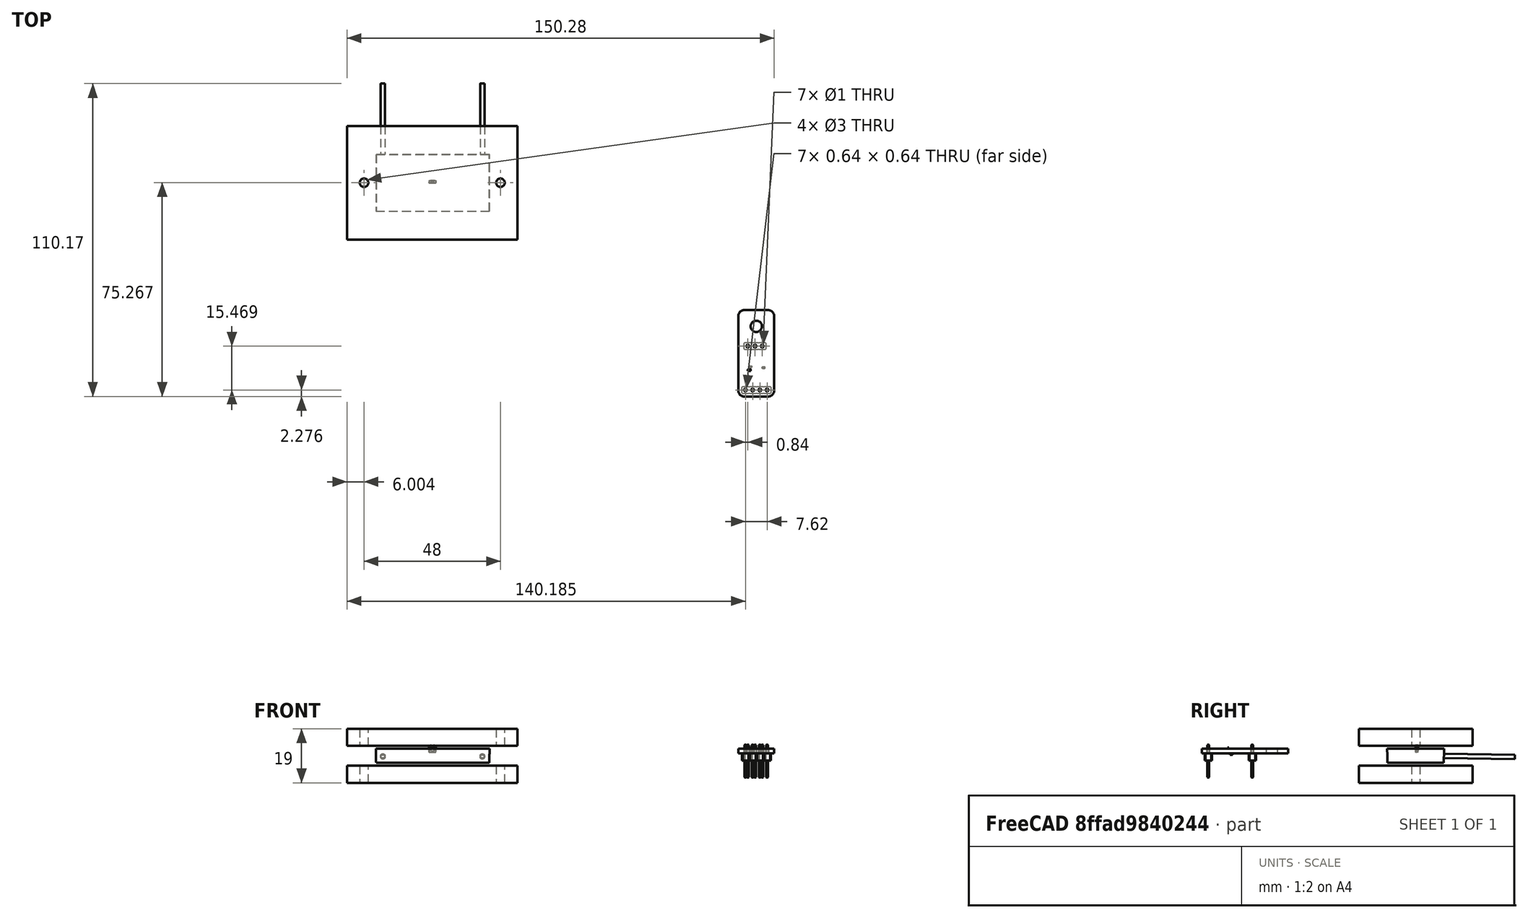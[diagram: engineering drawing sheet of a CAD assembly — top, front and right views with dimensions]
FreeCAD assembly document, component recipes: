
FREECAD ASSEMBLY — COMPONENT RECIPES ("Config-Peltier-SHT-31")

This assembly document has 4 components, labeled P0..P3 below (a component is one placed body or linked part). 3 of them carry a construction recipe — the FreeCAD feature program that regenerates the part from scratch, quoted from this document or its linked companion documents; the rest are supplied as boundary geometry only. No exploded tour is included for this assembly.
COMPONENT P0 — geometry summary ("SHT31-Breakout-rev01"; no construction recipe available for this part):
  bounding box: 30.4 x 12.6 x 3.0 mm
  tessellated surface: 10,052 triangles
  volume: 588 mm^3 (51% of its bounding box)
COMPONENT P1 — recipe-attached ("Placa-Sup", modeled in this document).
Construction recipe (the document's own serialized feature program — sketch geometry with constraints, then the solid features built on it; lengths are millimeters unless a unit is written):

FEATURE [Sketcher::SketchObject] Sketch
  FullyConstrained = true
  MapMode = 5
  Support = -> [XY_Plane]
  sketch-geometry (6):
    g0: Circle CenterX=-24.0764 CenterY=0.06715 CenterZ=0 NormalX=0 NormalY=0 NormalZ=1 AngleXU=0 Radius=1.5
    g1: Circle CenterX=23.9236 CenterY=0.06715 CenterZ=0 NormalX=0 NormalY=0 NormalZ=1 AngleXU=0 Radius=1.5
    g2: LineSegment StartX=-30.0764 StartY=20.0671 StartZ=0 EndX=29.9236 EndY=20.0671 EndZ=0
    g3: LineSegment StartX=29.9236 StartY=20.0671 StartZ=0 EndX=29.9236 EndY=-19.9329 EndZ=0
    g4: LineSegment StartX=29.9236 StartY=-19.9329 StartZ=0 EndX=-30.0764 EndY=-19.9329 EndZ=0
    g5: LineSegment StartX=-30.0764 StartY=-19.9329 StartZ=0 EndX=-30.0764 EndY=20.0671 EndZ=0
  constraints (18):
    c: Diameter(g1) = 3
    c: Diameter(g0) = 3
    c: Distance(g0,g-1) = 0.06715
    c: Coincident(g2,g3)
    c: Coincident(g3,g4)
    c: Coincident(g4,g5)
    c: Coincident(g5,g2)
    c: Horizontal(g2)
    c: Horizontal(g4)
    c: Vertical(g3)
    c: Vertical(g5)
    c: Distance(g3) = 40
    c: Distance(g2) = 60
    c: Distance(g1,g3) = 6
    c: Distance(g1,g2) = 20
    c: Distance(g0,g5) = 6
    c: Distance(g0,g2) = 20
    c: Block(g4)
FEATURE [PartDesign::Pad] Pad
  Direction = (0,0,1)
  Length = 6
  Length2 = 10
  Profile = -> Sketch
  ReferenceAxis = -> Sketch [N_Axis]
  Type = 0
FEATURE [PartDesign::Body] Body  label="Placa-Sup"
  Group = -> [Sketch,Pad]
  Origin = -> Origin
  Placement = pos=(0,0,1) rot=(0,0,1;0rad)
  Tip = -> Pad
COMPONENT P2 — recipe-attached ("Peltier", modeled in this document).
Construction recipe (the document's own serialized feature program — sketch geometry with constraints, then the solid features built on it; lengths are millimeters unless a unit is written):

FEATURE [PartDesign::Plane] DatumPlane
  Length = 60.9515
  MapMode = 5
  Placement = pos=(0,0,0) rot=(1,0,0;3.14159rad)
  ResizeMode = 0
  Width = 70.9193
FEATURE [Sketcher::SketchObject] Sketch002
  FullyConstrained = true
  MapMode = 5
  Placement = pos=(0,0,0) rot=(1,0,0;3.14159rad)
  Support = -> [DatumPlane]
  sketch-geometry (4):
    g0: LineSegment StartX=-19.909 StartY=9.99788 StartZ=0 EndX=20.091 EndY=9.99788 EndZ=0
    g1: LineSegment StartX=20.091 StartY=9.99788 StartZ=0 EndX=20.091 EndY=-10.0021 EndZ=0
    g2: LineSegment StartX=20.091 StartY=-10.0021 StartZ=0 EndX=-19.909 EndY=-10.0021 EndZ=0
    g3: LineSegment StartX=-19.909 StartY=-10.0021 StartZ=0 EndX=-19.909 EndY=9.99788 EndZ=0
  constraints (11):
    c: Coincident(g0,g1)
    c: Coincident(g1,g2)
    c: Coincident(g2,g3)
    c: Coincident(g3,g0)
    c: Horizontal(g0)
    c: Horizontal(g2)
    c: Vertical(g1)
    c: Vertical(g3)
    c: Distance(g0) = 40
    c: Distance(g1) = 20
    c: Block(g2)
FEATURE [PartDesign::Pad] Pad002
  Direction = (0,0,-1)
  Length = 5
  Length2 = 10
  Placement = pos=(0,0,0) rot=(1,0,0;3.14159rad)
  Profile = -> Sketch002
  ReferenceAxis = -> Sketch002 [N_Axis]
  TaperAngle = -1
  Type = 0
FEATURE [PartDesign::Plane] DatumPlane001
  Length = 61.1423
  MapMode = 45
  Placement = pos=(0.0910191,9.95852,-2.49818) rot=(0.58068,0.58068,0.570633;4.17868rad)
  ResizeMode = 0
  Support = -> [Pad002]
  Width = 60.1034
FEATURE [Sketcher::SketchObject] Sketch004
  FullyConstrained = true
  MapMode = 5
  Placement = pos=(0.0910191,9.95852,-2.49818) rot=(0.58068,0.58068,0.570633;4.17868rad)
  Support = -> [DatumPlane001]
  sketch-geometry (2):
    g0: Circle CenterX=0 CenterY=17.4497 CenterZ=0 NormalX=0 NormalY=0 NormalZ=1 AngleXU=0 Radius=0.75
    g1: Circle CenterX=0 CenterY=-17.5503 CenterZ=0 NormalX=0 NormalY=0 NormalZ=1 AngleXU=0 Radius=0.75
  constraints (6):
    c: Diameter(g0) = 1.5
    c: DistanceX(g-2,g0) = 0
    c: Block(g0)
    c: Diameter(g1) = 1.5
    c: DistanceX(g-2,g1) = 0
    c: DistanceY(g1,g0) = 35
FEATURE [PartDesign::Pad] Pad004
  BaseFeature = -> Pad002
  Direction = (0,0.999848,-0.0174524)
  Length = 25
  Length2 = 10
  Placement = pos=(0,0,0) rot=(1,0,0;3.14159rad)
  Profile = -> Sketch004
  ReferenceAxis = -> Sketch004 [N_Axis]
  Type = 0
FEATURE [PartDesign::Body] Body001  label="Peltier"
  Group = -> [DatumPlane,Sketch002,Pad002,DatumPlane001,Sketch004,Pad004]
  Origin = -> Origin001
  Tip = -> Pad004
COMPONENT P3 — recipe-attached ("Placa-Inf", modeled in this document).
Construction recipe (the document's own serialized feature program — sketch geometry with constraints, then the solid features built on it; lengths are millimeters unless a unit is written):

FEATURE [Sketcher::SketchObject] Sketch003
  FullyConstrained = true
  MapMode = 5
  Support = -> [XY_Plane002]
  sketch-geometry (6):
    g0: Circle CenterX=-24.0764 CenterY=0.06715 CenterZ=0 NormalX=0 NormalY=0 NormalZ=1 AngleXU=0 Radius=1.5
    g1: Circle CenterX=23.9236 CenterY=0.06715 CenterZ=0 NormalX=0 NormalY=0 NormalZ=1 AngleXU=0 Radius=1.5
    g2: LineSegment StartX=-30.0764 StartY=20.0671 StartZ=0 EndX=29.9236 EndY=20.0671 EndZ=0
    g3: LineSegment StartX=29.9236 StartY=20.0671 StartZ=0 EndX=29.9236 EndY=-19.9329 EndZ=0
    g4: LineSegment StartX=29.9236 StartY=-19.9329 StartZ=0 EndX=-30.0764 EndY=-19.9329 EndZ=0
    g5: LineSegment StartX=-30.0764 StartY=-19.9329 StartZ=0 EndX=-30.0764 EndY=20.0671 EndZ=0
  constraints (18):
    c: Diameter(g1) = 3
    c: Diameter(g0) = 3
    c: Distance(g0,g-1) = 0.06715
    c: Coincident(g2,g3)
    c: Coincident(g3,g4)
    c: Coincident(g4,g5)
    c: Coincident(g5,g2)
    c: Horizontal(g2)
    c: Horizontal(g4)
    c: Vertical(g3)
    c: Vertical(g5)
    c: Distance(g3) = 40
    c: Distance(g2) = 60
    c: Distance(g1,g3) = 6
    c: Distance(g1,g2) = 20
    c: Distance(g0,g5) = 6
    c: Distance(g0,g2) = 20
    c: Block(g4)
FEATURE [PartDesign::Pad] Pad003
  Direction = (0,0,1)
  Length = 6
  Length2 = 10
  Profile = -> Sketch003
  ReferenceAxis = -> Sketch003 [N_Axis]
  Type = 0
FEATURE [PartDesign::Body] Body002  label="Placa-Inf"
  Group = -> [Sketch003,Pad003]
  Origin = -> Origin002
  Placement = pos=(0,0,-12) rot=(0,0,1;0rad)
  Tip = -> Pad003
PROVENANCE & LICENSES
A FreeCAD (.FCStd) document from a public repository crawl; recipes are the document's own serialized feature recipes (and, for linked parts, companion documents' recipes).
License: mit.
